# Revit family: ledspotprojector-e_rd127-15w-830-36d_709000027400
name_source: partatom
category: Leuchten
revit_build: Autodesk Revit 2016 (Build: 20190508_0715(x64)
units: mm (PartAtom-declared; Revit-internal decimal feet)

## family parameters
Basisbauteil = Fläche
Beim Laden mit Abzugskörper schneiden = Nein
Bemaßung runder Anschluss = Durchmesser verwenden
Gemeinsam genutzt = Nein
Lichtquelle = Nein
Raumberechnungspunkt = Nein
Teiletyp = Normal

## types (1)
- LEDSpotProjector-E Rd127-15W-830-36D (1 x LED, 1200 lm)
    Approval mark = CE
    Beschreibung = Stylish outdoor spot . Sleek award-winning design. Suitable for illuminating walls and signages or highlighting objects in parks and gardens. IP66 water resistance level and IK07 impact protection. Adjustable tilting angle of 180°. Die casted aluminium body. 1.5 meter cable for convenient connection. Earth spike accessory available.
    CIE Flux Codes = 95 99 100 100 99
    Control Gear = Electronic ballast
    Height = 0 mm  [stored 0 ft]
    Hersteller = OPPLE
    Lamp Light Flux = 1200 lm
    Lamp count = 1
    Lampe = 1 x LED
    Length = 104 mm  [stored 0.341207 ft]
    Luminous efficacy = 76 lm/W
    ModVariant = Nein
    Modell = 709000027400
    Mounting Place = Floor
    Mounting Type = Surface mounted
    Number of Poles = 1
    OnlyDefault = Ja
    Power Factor = 1
    Product Name = LEDSpotProjector-E Rd127-15W-830-36D
    Product group = Spot Projector
    ProductGroupID = 3332
    Protection Class = Protection class I
    Protection Degree = IP 66
    RLX_Detail_Level = 1
    RlxData = <blob elided: 148077 chars, md5=a230aa8c>
    Scheinlast = 16 VA
    Socket = socket
    Standby Power = 0 W
    System Light Flux = 1183 lm
    System Power = 16 W
    Typenbild = 709000027400.jpg
    Typenkommentare = Product without accessories
    URL = http://relux.com
    VarID = ---
    Voltage = 0 V
    Vorgabe-Ansicht = 1800 mm
    Weight = 0.00 kg
    Width = 0 mm  [stored 0 ft]

note: [stored X ft] marks values corroborated as IEEE doubles in the binary element streams (Revit-internal decimal feet)

## geometry (parser evidence)
native form markers: Blend x4, Sweep x16
no freeform markers — native parametric forms only
